# Revit family: Receptor_Sani-Flor_16_In_Square_7_In_Sump-Zurn-Z1920
name_source: partatom
category: Plumbing Fixtures
units: mm (PartAtom-declared; Revit-internal decimal feet)

## family parameters
Always vertical = Yes
Cut with Voids When Loaded = No
Maintain Annotation Orientation = No
OmniClass Number = 23.45.05.14.14
OmniClass Title = Sinks/Lavatories
Part Type = Normal
Room Calculation Point = No
Round Connector Dimension = Use Radius
Shared = No
Work Plane-Based = No

## types (16) — shared parameters
Approx. Weight (Lbs) = 81 "
Assembly Code = D2030300
CW Connection = No
Default Elevation = 4 "
Description = 16 X 16 [406 X 406] A.R.C. SANI-FLOR RECEPTOR 7 [178] SUMP DEPTH
Grate Open Area (Sq. In) = 54
HW Connection = No
Main Material = Iron - Zurn - Cast - Painted - White A.R.E Coated
Manufacturer = Zurn Water, LLC
Manufacurer Brand = Zurn
Modified Date = 12/29/2025
Product Documentation Link = https://files.zurn.com
Product Page URL = https://www.zurn.com
Product data url = https://www.bimobject.com
Thickness = 0.25 "
Trap Primer = Yes
URL = www.zurn.com
Vent Connection = No
WFU = 1
Waste Connection = Yes
zero-valued in all types: CWFU, HWFU

## per-type parameters (varying)
| type | A_ Pipe Size (Actual-Inner) | A_ Pipe Size (Actual-Outer) | A_ Pipe Size (Nominal) | Connector Radius | E_ Body Length | E_ Body Length_Derived | Grate Material | Top size | Type Comments | ZN Top | ZN-Top Height |
| Z1920-2IC | 2.067 " | 2.375 " | 2 " | 1 " | 9.75 " | 9.75 " | Iron - Zurn - Cast - Painted - White A.R.E Coated | 16 " | Z1920 Sani-Flor Receptor 2 Inch Inside Caulk Outlet | No | 0 " |
| Z1920-3IC | 3.068 " | 3.5 " | 3 " | 1.5 " | 9.75 " | 9.75 " | Iron - Zurn - Cast - Painted - White A.R.E Coated | 16 " | Z1920 Sani-Flor Receptor 3 Inch Inside Caulk Outlet | No | 0 " |
| Z1920-4IC | 4.026 " | 4.5 " | 4 " | 2 " | 9.75 " | 9.75 " | Iron - Zurn - Cast - Painted - White A.R.E Coated | 16 " | Z1920 Sani-Flor Receptor 4 Inch Inside Caulk Outlet | No | 0 " |
| Z1920-6IC | 6.065 " | 6.625 " | 6 " | 3 " | 9.75 " | 9.75 " | Iron - Zurn - Cast - Painted - White A.R.E Coated | 16 " | Z1920 Sani-Flor Receptor 6 Inch Inside Caulk Outlet | No | 0 " |
| Z1920-8IC | 7.981 " | 8.625 " | 8 " | 4 " | 10.25 " | 10.25 " | Iron - Zurn - Cast - Painted - White A.R.E Coated | 16 " | Z1920 Sani-Flor Receptor 8 Inch Inside Caulk Outlet | No | 0 " |
| Z1920-2NL | 2.067 " | 2.375 " | 2 " | 1 " | 9 " | 9 " | Iron - Zurn - Cast - Painted - White A.R.E Coated | 16 " | Z1920 Sani-Flor Receptor 2 Inch Neo-Loc Outlet | No | 0 " |
| Z1920-3NL | 3.068 " | 3.5 " | 3 " | 1.5 " | 9 " | 9 " | Iron - Zurn - Cast - Painted - White A.R.E Coated | 16 " | Z1920 Sani-Flor Receptor 3 Inch Neo-Loc Outlet | No | 0 " |
| Z1920-4NL | 4.026 " | 4.5 " | 4 " | 2 " | 9 " | 9 " | Iron - Zurn - Cast - Painted - White A.R.E Coated | 16 " | Z1920 Sani-Flor Receptor 4 Inch Neo-Loc Outlet | No | 0 " |
| ZN1920-2IC | 2.067 " | 2.375 " | 2 " | 1 " | 9.938 " | 9.75 " | Bronze - Zurn - Polished Nickel | 16.75 " | ZN1920 Sani-Flor Receptor 2 Inch Inside Caulk Outlet | Yes | 0.188 " |
| ZN1920-3IC | 3.068 " | 3.5 " | 3 " | 1.5 " | 9.938 " | 9.75 " | Bronze - Zurn - Polished Nickel | 16.75 " | ZN1920 Sani-Flor Receptor 3 Inch Inside Caulk Outlet | Yes | 0.188 " |
| ZN1920-4IC | 4.026 " | 4.5 " | 4 " | 2 " | 9.938 " | 9.75 " | Bronze - Zurn - Polished Nickel | 16.75 " | ZN1920 Sani-Flor Receptor 4 Inch Inside Caulk Outlet | Yes | 0.188 " |
| ZN1920-6IC | 6.065 " | 6.625 " | 6 " | 3 " | 9.938 " | 9.75 " | Bronze - Zurn - Polished Nickel | 16.75 " | ZN1920 Sani-Flor Receptor 6 Inch Inside Caulk Outlet | Yes | 0.188 " |
| ZN1920-8IC | 7.981 " | 8.625 " | 8 " | 4 " | 10.438 " | 10.25 " | Bronze - Zurn - Polished Nickel | 16.75 " | ZN1920 Sani-Flor Receptor 8 Inch Inside Caulk Outlet | Yes | 0.188 " |
| ZN1920-2NL | 2.067 " | 2.375 " | 2 " | 1 " | 9.188 " | 9 " | Bronze - Zurn - Polished Nickel | 16.75 " | ZN1920 Sani-Flor Receptor 2 Inch Neo-Loc Outlet | Yes | 0.188 " |
| ZN1920-3NL | 3.068 " | 3.5 " | 3 " | 1.5 " | 9.188 " | 9 " | Bronze - Zurn - Polished Nickel | 16.75 " | ZN1920 Sani-Flor Receptor 3 Inch Neo-Loc Outlet | Yes | 0.188 " |
| ZN1920-4NL | 4.026 " | 4.5 " | 4 " | 2 " | 9.188 " | 9 " | Bronze - Zurn - Polished Nickel | 16.75 " | ZN1920 Sani-Flor Receptor 4 Inch Neo-Loc Outlet | Yes | 0.188 " |

note: column(s) folded — value = type name in every type: Model

## geometry (parser evidence)
native form markers: Sweep x6
no freeform markers — native parametric forms only
